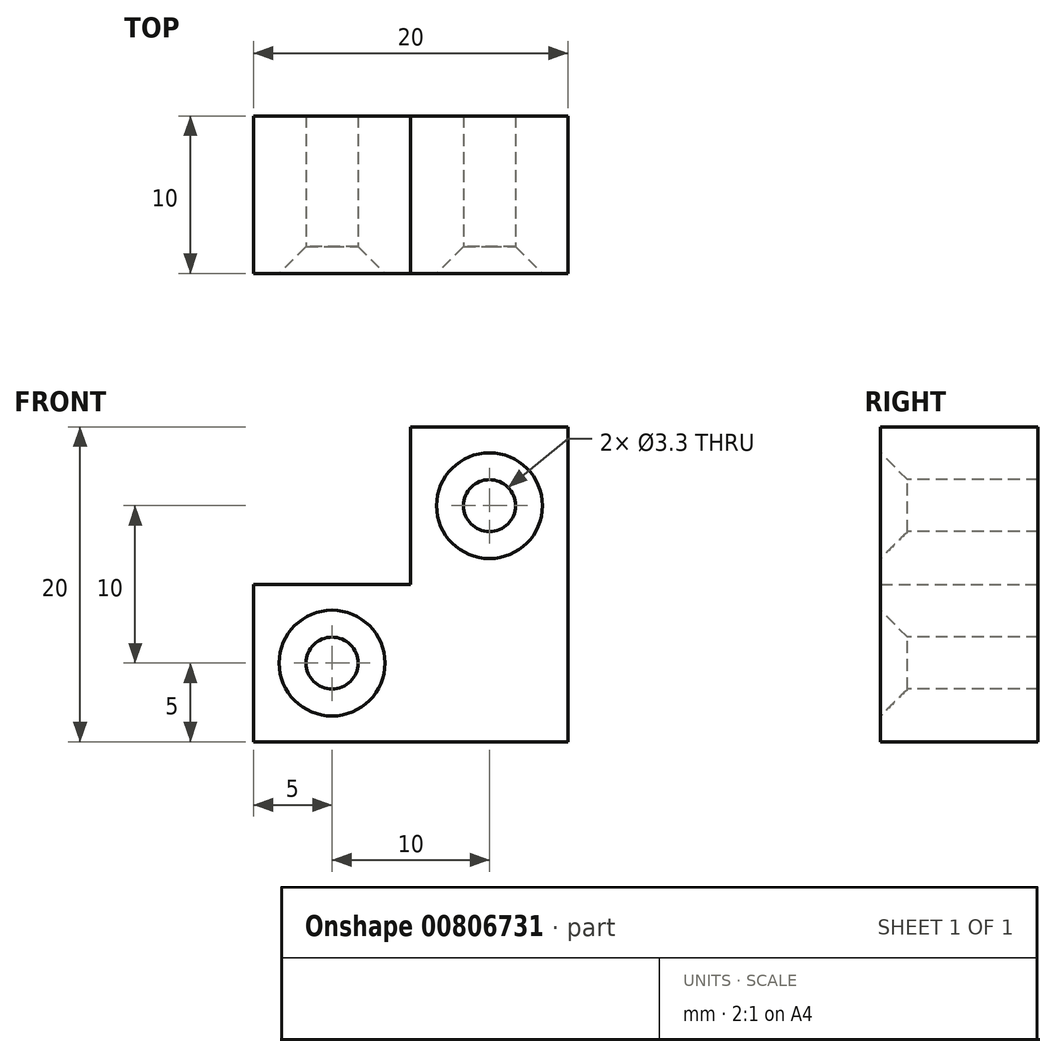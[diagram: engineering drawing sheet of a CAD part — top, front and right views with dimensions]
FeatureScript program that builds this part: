
annotation { "Feature Type Name" : "Feature", "Feature Type Description" : "" }
export const myFeature = defineFeature(function(context is Context, id is Id, definition is map)
    precondition{}
    {
        {
            var Q0;
            Q0=qCreatedBy(makeId("Front.planeOp"),FACE);
            var sketch = newSketch(context, id + "F0", { "sketchPlane" : qUnion([Q0])});
            skLineSegment(sketch, "E0", {"start": v(-10, 20) * mm, "end": v(0, 20) * mm});
            skLineSegment(sketch, "E1", {"start": v(0, 20) * mm, "end": v(0, 0) * mm});
            skLineSegment(sketch, "E2", {"start": v(0, 0) * mm, "end": v(-20, 0) * mm});
            skLineSegment(sketch, "E3", {"start": v(-20, 0) * mm, "end": v(-20, 10) * mm});
            skLineSegment(sketch, "E4", {"start": v(-20, 10) * mm, "end": v(-10, 10) * mm});
            skLineSegment(sketch, "E5", {"start": v(-10, 10) * mm, "end": v(-10, 20) * mm});
            skSolve(sketch);
        }
        {
            var Q0;
            Q0 = qSketchRegion(id + "F0", true);
            extrude(context, id + "F1", {"entities" : qUnion([Q0]), "depth" : 10 * mm, "offsetDistance" : 25 * mm});
        }
        {
            var Q0;
            Q0=makeQuery(id+"F1.opExtrude","CAP_FACE",FACE,{"disambiguationData":[OSD([sQuery(id+"F0.wireOp",EDGE,"E0"),sQuery(id+"F0.wireOp",EDGE,"E1"),sQuery(id+"F0.wireOp",EDGE,"E2"),sQuery(id+"F0.wireOp",EDGE,"E3"),sQuery(id+"F0.wireOp",EDGE,"E4"),sQuery(id+"F0.wireOp",EDGE,"E5")])],"isStart":false});
            var sketch = newSketch(context, id + "F2", { "sketchPlane" : qUnion([Q0])});
            skPoint(sketch, "E6", {"position": v(-5, 15) * mm});
            skPoint(sketch, "E7", {"position": v(-15, 5) * mm});
            skLineSegment(sketch, "E8", {"start": v(-5, 15) * mm, "end": v(-5, 20) * mm, "construction": true});
            skLineSegment(sketch, "E9", {"start": v(-5, 15) * mm, "end": v(-10, 15) * mm, "construction": true});
            skSolve(sketch);
        }
        {
            var Q0;
            Q0=sQuery(id+"F2.wireOp",VERTEX,"E6");
            var Q1;
            Q1=sQuery(id+"F2.wireOp",VERTEX,"E7");
            var Q2;
            Q2=makeQuery(id+"F1.opExtrude","SWEPT_BODY",BODY,{"disambiguationData":[OSD([sQuery(id+"F0.wireOp",EDGE,"E0"),sQuery(id+"F0.wireOp",EDGE,"E1"),sQuery(id+"F0.wireOp",EDGE,"E2"),sQuery(id+"F0.wireOp",EDGE,"E3"),sQuery(id+"F0.wireOp",EDGE,"E4"),sQuery(id+"F0.wireOp",EDGE,"E5")])]});
            hole(context, id + "F3", {"style" : HoleStyle.C_SINK, "endStyle" : HoleEndStyle.THROUGH, "standardTappedOrClearance" : lookupTablePath({ "standard" : "ISO", "fit" : "Normal", "size" : "M3", "type" : "Clearance" }), "standardBlindInLast" : lookupTablePath({ "fit" : "Standard", "standard" : "ISO", "size" : "M3", "type" : "Clearance" }), "holeDiameter" : 3.3 * mm, "cSinkDiameter" : 6.72 * mm, "cSinkAngle" : 90 * degree, "majorDiameter" : 5 * mm, "isTappedThrough" : true, "tappedDepth" : 8 * mm, "tapClearance" : 3, "startFromSketch" : true, "locations" : qUnion([Q0, Q1]), "scope" : qUnion([Q2])});
        }
    });
